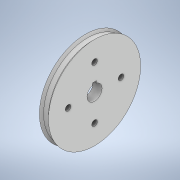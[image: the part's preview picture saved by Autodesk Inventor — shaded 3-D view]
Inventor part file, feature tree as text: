
AUTODESK INVENTOR PART (.ipt)
format: ipt  version: 2022 (Build 260153000, 153)  size: 144,896 bytes
history: native  units: mm
features: sketch x3, extrude x2, thicken_offset x2, revolve x1
ambient origin geometry x8: Origin, YZ Plane, XZ Plane, XY Plane, X Axis, Y Axis, Z Axis, Center Point
bodies: Solid1 (feature_tree)
feature tree (8):
  revolve  "Revolution1"  Angle=360.0deg
  extrude  "Extrusion1"  Depth=10.0mm
  thicken_offset  "Thicken1"
  thicken_offset  "Thicken2"
  extrude  "Extrusion2"  Depth=10.0mm
  sketch  "Sketch1"  dims[d8=90.0deg d10=40.0mm d12=360.0deg]
  sketch  "Sketch2"  dims[d14=0.0mm d15=0.0mm d16=10.0mm]
  sketch  "Sketch3"  dims[d17=10.0mm d18=10.0mm d19=10.0mm d22=0.0mm d23=0.0mm d20=14.3117mm d21=0.75mm d24=0.75mm d25=0.375mm]
